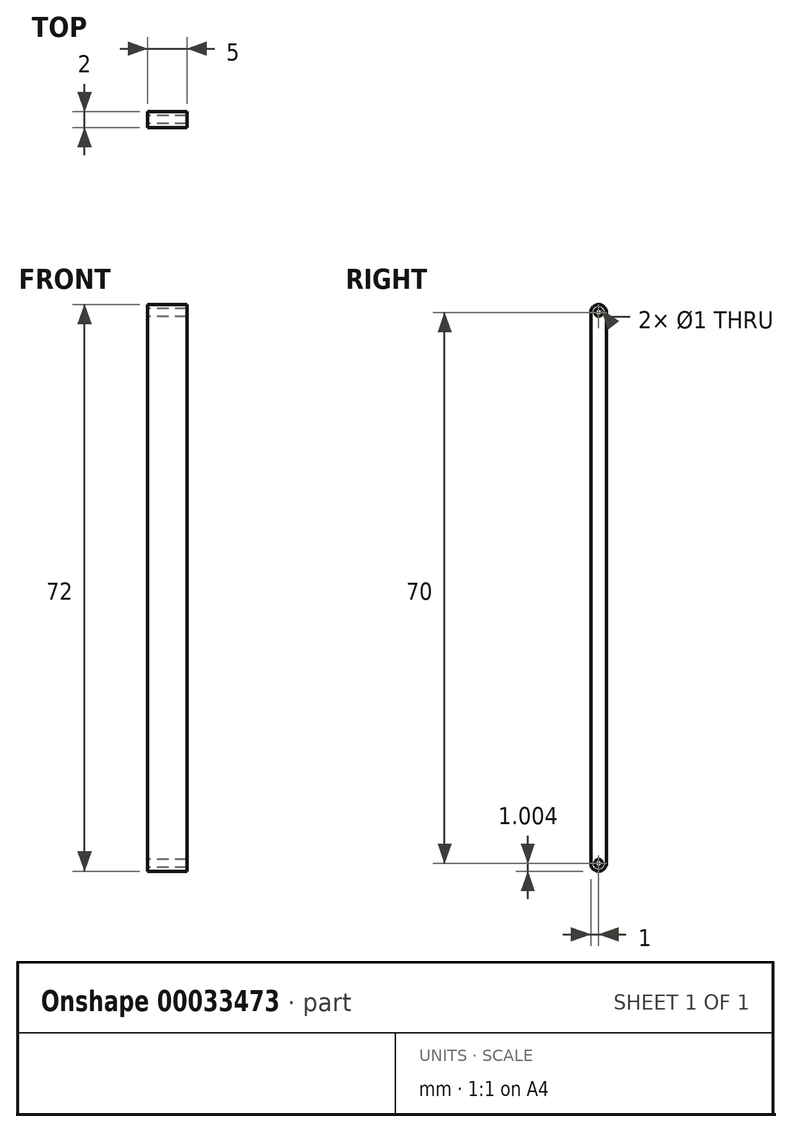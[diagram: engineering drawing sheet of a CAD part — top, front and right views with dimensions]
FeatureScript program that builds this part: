
annotation { "Feature Type Name" : "Feature", "Feature Type Description" : "" }
export const myFeature = defineFeature(function(context is Context, id is Id, definition is map)
    precondition{}
    {
        {
            var Q0;
            Q0=qCreatedBy(makeId("Right.planeOp"),FACE);
            var sketch = newSketch(context, id + "F0", { "sketchPlane" : qUnion([Q0])});
            skLineSegment(sketch, "E0.left", {"start": v(0, 4.95) * mm, "end": v(0, -65.05) * mm});
            skLineSegment(sketch, "E0.right", {"start": v(-2, 4.95) * mm, "end": v(-2, -65.05) * mm});
            skArc(sketch, "E1", {"start": v(0, 4.95) * mm, "mid": v(-1, 5.95) * mm, "end": v(-2, 4.95) * mm});
            skArc(sketch, "E2", {"start": v(-2, -65.05) * mm, "mid": v(-1, -66.05) * mm, "end": v(0, -65.05) * mm});
            skCircle(sketch, "E3", {"center": v(-1, 4.95) * mm, "radius": 0.5 * mm});
            skCircle(sketch, "E4", {"center": v(-1, -65.05) * mm, "radius": 0.5 * mm});
            skSolve(sketch);
        }
        {
            var Q0;
            Q0=makeQuery(id+"F0.imprint","IMPRINT",FACE,{"disambiguationData":[TD([[makeQuery(id+"F0.imprint","IMPRINT",EDGE,{"derivedFrom":sQuery(id+"F0.wireOp",EDGE,"E0.left")}),-1.0]])]});
            extrude(context, id + "F1", {"entities" : qUnion([Q0]), "depth" : 5 * mm});
        }
    });
